# Revit family: Gira_102300
name_source: partatom
category: Elektroinstallationen
revit_build: Autodesk Revit 2017 (Build: 20160225_1515(x64)
units: mm (PartAtom-declared; Revit-internal decimal feet)

## family parameters
Basisbauteil = Fläche
Beim Laden mit Abzugskörper schneiden = Nein
Bemaßung runder Anschluss = Durchmesser verwenden
Beschriftungsausrichtung beibehalten = Nein
Gemeinsam genutzt = Nein
Raumberechnungspunkt = Nein
Teiletyp = Normal

## types (1)
- Gira_102300
    Andere Bussysteme = ohne
    BIM = https://media.stage.bim.site X1 REG KNX.rfa
    Beschreibung = KNX Bereichs- Linienkoppler bzw. Linienverstärker  REG plus Merkmale: - Der Bereichs- Linienkoppler verbindet datentechnisch zwei KNX Linien miteinander und gewährleistet eine galvanische Trennung zwischen diesen Linien. Dadurch kann jede Buslinie einer KNX Installation elektrisch unabhängig von den anderen Linien betrieben werden. Bereichs- Linienkoppler: - Einsatz als Bereichs- oder Linienkoppler je nach Vergabe der physikalischen Adresse und Parametrierung. - Verringerung der Busbelastung durch Filterfunktion (Filtertabelle). - Weiterleitung von Gruppentelegrammen parametrierbar. - Wiederholungsrate bei Übertragungsfehlern. - Telegrammbestätigung parametrierbar. - Unterstützung des vollständig erweiterten Gruppenadressbereichs von 0 bis 31 mit den Funktionen sperren", "ungefiltert weiterleiten" und "filtern" in beide Kommunikationsrichtungen zwischen Haupt- und Unterlinie. - Funktion "ungefiltert weiterleiten" und "sperren" auch für physikalisch adressierte Telegramme zwischen Haupt- und Unterlinie in beide Kommunikationsrichtungen auswählbar (Programmier- und Sabotageschutz). - Funktion "Wiederholung : ja nein" bei Übertragungsfehlern auf der Haupt- bzw. Unterlinie für die Telegrammart "Broadcast" separat einstellbar. - Telegrammbestätigung auf der Haupt- bzw. Unterlinie mit den Einstellungen "immer" und "nur bei Weiterleitung" separat für Gruppentelegramme und physikalisch adressierte Telegramme möglich. - Für physikalisch adressierte Telegramme ist die Einstellung "immer abweisen NACK (Not-Acknowledge)" auswählenbar (Programmierschutz mit Rückmeldung). Linienverstärker: - Als Linienverstärker ist die Erweiterung von Linien auf max. vier Liniensegmente (max. drei parallelgeschaltete Linienverstärker pro Linie) mit jeweils bis zu 64 Teilnehmern möglich. - Wiederholungsrate bei Übertragungsfehlern.  Hinweise : - Für jede Linie (Bereichslinie, Hauptlinie, Linie) bzw. jedes Liniensegment ist eine separate Spannungsversorgung notwendig."
    Breite in Teilungseinheiten = 2
    Bussystem Funkbus = Nein
    Bussystem KNX = Ja
    Bussystem KNX-Funk = Nein
    Bussystem LON = Nein
    Bussystem Powernet = Nein
    Datenblatt = https://katalog.gira.de
    GTIN = 4010337040798
    HAN = 102300
    Hersteller = Gira
    Logischer Baustein = Ja
    Mit Busankopplung = Nein
    Montageart = REG
    Produktseite = http://katalog.gira.de
    Typname = Bereichs-/Linienkoppler Linienverstärker KNX REG
    URL = https://www.gira.de
    Vorgabe-Ansicht = 1219 mm

## geometry (parser evidence)
native form markers: Sweep x2
no freeform markers — native parametric forms only
